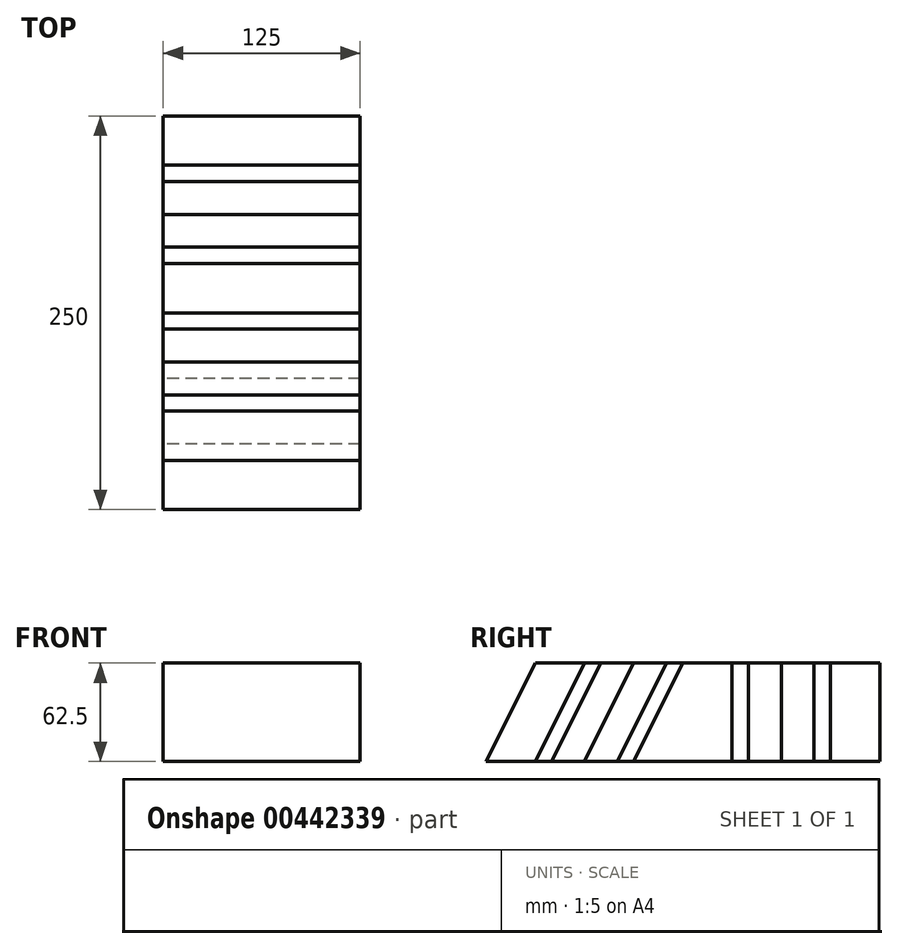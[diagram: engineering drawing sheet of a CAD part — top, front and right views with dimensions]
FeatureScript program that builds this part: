
annotation { "Feature Type Name" : "Feature", "Feature Type Description" : "" }
export const myFeature = defineFeature(function(context is Context, id is Id, definition is map)
    precondition{}
    {
        {
            var Q0;
            Q0=qCreatedBy(makeId("Front.planeOp"),FACE);
            var sketch = newSketch(context, id + "F0", { "sketchPlane" : qUnion([Q0])});
            skLineSegment(sketch, "E0.bottom", {"start": v(62.5, 31.25) * mm, "end": v(-62.5, 31.25) * mm});
            skLineSegment(sketch, "E0.top", {"start": v(62.5, -31.25) * mm, "end": v(-62.5, -31.25) * mm});
            skLineSegment(sketch, "E0.left", {"start": v(62.5, 31.25) * mm, "end": v(62.5, -31.25) * mm});
            skLineSegment(sketch, "E0.right", {"start": v(-62.5, 31.25) * mm, "end": v(-62.5, -31.25) * mm});
            skPoint(sketch, "E0.middle", {"position": v(0, 0) * mm});
            skSolve(sketch);
        }
        {
            var Q0;
            Q0=makeQuery(id+"F0.imprint","IMPRINT",FACE,{"disambiguationData":[TD([[makeQuery(id+"F0.imprint","IMPRINT",EDGE,{"derivedFrom":sQuery(id+"F0.wireOp",EDGE,"E0.bottom")}),1.0]])]});
            extrude(context, id + "F1", {"entities" : qUnion([Q0]), "endBound" : BoundingType.SYMMETRIC, "depth" : 250 * mm});
        }
        {
            var Q0;
            Q0=qSketchRegion(id+"F0",true);
            extrude(context, id + "F2", {"entities" : qUnion([Q0]), "endBound" : BoundingType.SYMMETRIC, "depth" : 125 * mm});
        }
        {
            var Q0;
            Q0=makeQuery(id+"F0.imprint","IMPRINT",FACE,{"disambiguationData":[TD([[makeQuery(id+"F0.imprint","IMPRINT",EDGE,{"derivedFrom":sQuery(id+"F0.wireOp",EDGE,"E0.bottom")}),1.0]])]});
            extrude(context, id + "F3", {"entities" : qUnion([Q0]), "endBound" : BoundingType.SYMMETRIC, "depth" : (250 * 3 / 4) * mm});
        }
        {
            var Q0;
            Q0=makeQuery(id+"F0.imprint","IMPRINT",FACE,{"disambiguationData":[TD([[makeQuery(id+"F0.imprint","IMPRINT",EDGE,{"derivedFrom":sQuery(id+"F0.wireOp",EDGE,"E0.bottom")}),1.0]])]});
            extrude(context, id + "F4", {"entities" : qUnion([Q0]), "endBound" : BoundingType.SYMMETRIC, "depth" : (250 / 4) * mm});
        }
        {
            var Q0;
            Q0=makeQuery(id+"F0.imprint","IMPRINT",FACE,{"disambiguationData":[TD([[makeQuery(id+"F0.imprint","IMPRINT",EDGE,{"derivedFrom":sQuery(id+"F0.wireOp",EDGE,"E0.bottom")}),1.0]])]});
            extrude(context, id + "F5", {"entities" : qUnion([Q0]), "endBound" : BoundingType.SYMMETRIC, "depth" : 250 * 2 / 3 * mm});
        }
        {
            var Q0;
            Q0=makeQuery(id+"F0.imprint","IMPRINT",FACE,{"disambiguationData":[TD([[makeQuery(id+"F0.imprint","IMPRINT",EDGE,{"derivedFrom":sQuery(id+"F0.wireOp",EDGE,"E0.bottom")}),1.0]])]});
            extrude(context, id + "F6", {"entities" : qUnion([Q0]), "endBound" : BoundingType.SYMMETRIC, "depth" : (250 / 3) * mm});
        }
        {
            var Q0;
            Q0=makeQuery(id+"F1.opExtrude","CAP_EDGE",EDGE,{"disambiguationData":[OSD([sQuery(id+"F0.wireOp",EDGE,"E0.bottom")])],"isStart":false});
            chamfer(context, id + "F7", {"entities" : qUnion([Q0]), "chamferType" : ChamferType.TWO_OFFSETS, "width1" : 62.5 * mm, "oppositeDirection" : false, "width2" : 31.25 * mm, "tangentPropagation" : true});
        }
        {
            var Q0;
            Q0=makeQuery(id+"F2.opExtrude","CAP_EDGE",EDGE,{"disambiguationData":[OSD([sQuery(id+"F0.wireOp",EDGE,"E0.bottom")])],"isStart":false});
            chamfer(context, id + "F8", {"entities" : qUnion([Q0]), "chamferType" : ChamferType.TWO_OFFSETS, "width1" : 62.5 * mm, "oppositeDirection" : false, "width2" : 31.25 * mm, "tangentPropagation" : true});
        }
        {
            var Q0;
            Q0=makeQuery(id+"F3.opExtrude","CAP_EDGE",EDGE,{"disambiguationData":[OSD([sQuery(id+"F0.wireOp",EDGE,"E0.bottom")])],"isStart":false});
            chamfer(context, id + "F9", {"entities" : qUnion([Q0]), "chamferType" : ChamferType.TWO_OFFSETS, "width1" : 62.5 * mm, "oppositeDirection" : false, "width2" : 31.25 * mm, "tangentPropagation" : true});
        }
        {
            var Q0;
            Q0=makeQuery(id+"F5.opExtrude","CAP_EDGE",EDGE,{"disambiguationData":[OSD([sQuery(id+"F0.wireOp",EDGE,"E0.bottom")])],"isStart":false});
            chamfer(context, id + "F10", {"entities" : qUnion([Q0]), "chamferType" : ChamferType.TWO_OFFSETS, "width1" : 62.5 * mm, "oppositeDirection" : false, "width2" : 31.25 * mm, "tangentPropagation" : true});
        }
        {
            var Q0;
            Q0=makeQuery(id+"F4.opExtrude","CAP_EDGE",EDGE,{"disambiguationData":[OSD([sQuery(id+"F0.wireOp",EDGE,"E0.bottom")])],"isStart":false});
            chamfer(context, id + "F11", {"entities" : qUnion([Q0]), "chamferType" : ChamferType.TWO_OFFSETS, "width1" : 62.5 * mm, "oppositeDirection" : false, "width2" : 31.25 * mm, "tangentPropagation" : true});
        }
        {
            var Q0;
            Q0=makeQuery(id+"F6.opExtrude","CAP_EDGE",EDGE,{"disambiguationData":[OSD([sQuery(id+"F0.wireOp",EDGE,"E0.bottom")])],"isStart":false});
            chamfer(context, id + "F12", {"entities" : qUnion([Q0]), "chamferType" : ChamferType.TWO_OFFSETS, "width1" : 62.5 * mm, "oppositeDirection" : false, "width2" : 31.25 * mm, "tangentPropagation" : true});
        }
    });
